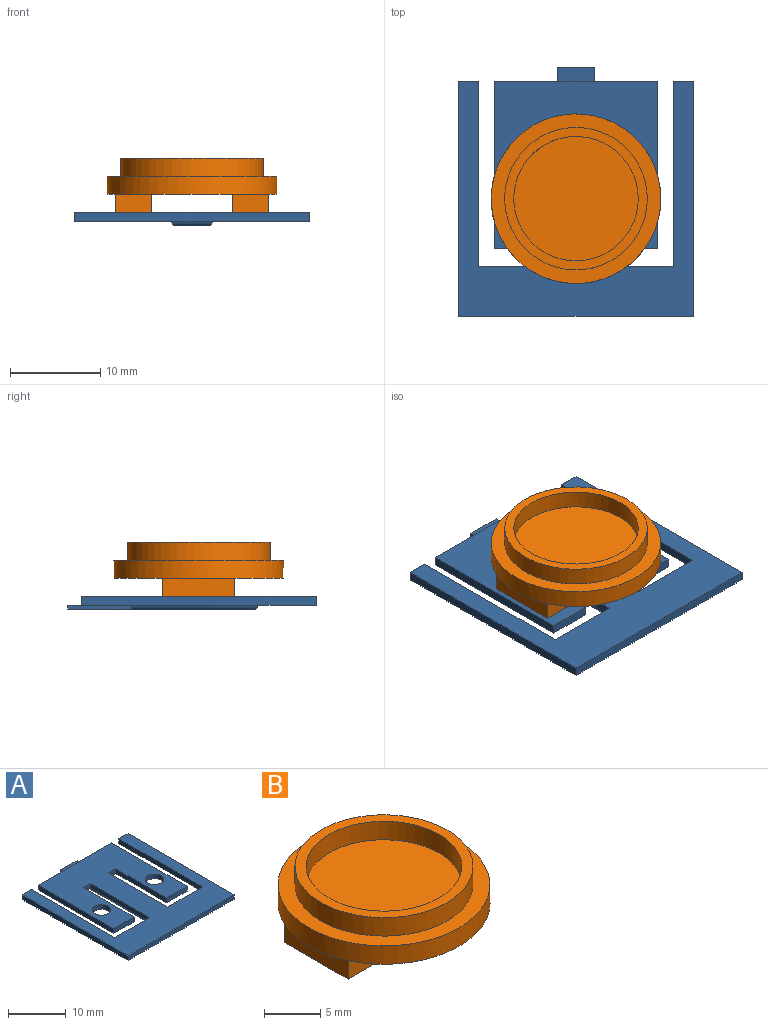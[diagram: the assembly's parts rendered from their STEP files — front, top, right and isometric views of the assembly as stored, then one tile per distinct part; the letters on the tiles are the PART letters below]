
ASSEMBLY  parts=2 mates=1
PART A: 36 faces, bbox 26x27.5x1.5 mm
  f0: plane 26x26mm, normal (0,0,-1), area 239.8mm2, adj f2,f3,f4,f5,f6,f7,f8,f18
  f1: plane 18.5x7mm, normal (0,0,-1), area 96.3mm2, adj f13,f14,f15,f16,f17,f21,f26,f27
  f2: plane 26x1mm, normal (-1,0,0), area 26mm2, adj f0,f3,f23,f24
  f3: plane 26x1mm, normal (0,-1,0), area 26mm2, adj f0,f2,f4,f24
  f4: plane 26x1mm, normal (1,0,0), area 26mm2, adj f0,f3,f5,f24
  f5: plane 2.25x1mm, normal (0,1,0), area 2.2mm2, adj f0,f4,f6,f24
  f6: plane 20.5x1mm, normal (-1,0,0), area 20.5mm2, adj f0,f5,f7,f24
  f7: plane 8.5x1mm, normal (0,1,0), area 8.5mm2, adj f0,f6,f8,f24
  f8: plane 14.5x1mm, normal (1,0,0), area 14.5mm2, adj f0,f7,f9,f24,f35
  f9: plane 1.75x1mm, normal (0,-1,0), area 1.8mm2, adj f8,f10,f24,f25
  f10: plane 12.5x1mm, normal (-1,0,0), area 12.5mm2, adj f9,f11,f24,f25
  f11: plane 5x1mm, normal (0,-1,0), area 5mm2, adj f10,f12,f24,f25
  f12: plane 18.5x1mm, normal (1,0,0), area 18.5mm2, adj f11,f13,f24,f25
  f13: plane 18x1mm, normal (0,1,0), area 18mm2, adj f1,f12,f14,f24,f25,f32
  f14: plane 18.5x1mm, normal (-1,0,0), area 18.5mm2, adj f1,f13,f15,f24
  f15: plane 5x1mm, normal (0,-1,0), area 5mm2, adj f1,f14,f16,f24
  f16: plane 12.5x1mm, normal (1,0,0), area 12.5mm2, adj f1,f15,f17,f24
  f17: plane 1.75x1mm, normal (0,-1,0), area 1.7mm2, adj f1,f16,f18,f24
  f18: plane 14.5x1mm, normal (-1,0,0), area 14.5mm2, adj f0,f17,f19,f24,f33
  f19: plane 8.5x1mm, normal (0,1,0), area 8.5mm2, adj f0,f18,f20,f24
  f20: plane 20.5x1mm, normal (1,0,0), area 20.5mm2, adj f0,f19,f23,f24
  f21: cylinder r=1.6mm len=3.2mm, axis (0,0,-1), area 10.1mm2, adj f1,f24
  f22: cylinder r=1.6mm len=3.2mm, axis (0,0,-1), area 10.1mm2, adj f24,f25
  f23: plane 2.25x1mm, normal (0,1,0), area 2.3mm2, adj f0,f2,f20,f24
  f24: plane 26x26mm, normal (0,0,1), area 517.4mm2, adj f2,f3,f4,f5,f6,f7,f8,f9
  f25: plane 18.5x7mm, normal (0,0,-1), area 96.3mm2, adj f9,f10,f11,f12,f13,f22,f29,f30
  f26: plane 0.43x0.25mm, normal (0,1,0), area 0.1mm2, adj f1,f27,f33
  f27: plane 7x0.43mm, normal (-1,0,0), area 3mm2, adj f1,f26,f28,f32,f33
  f28: plane 4x0.5mm, normal (0,1,0), area 2mm2, adj f27,f29,f31,f32,f33,f35
  f29: plane 7x0.43mm, normal (1,0,0), area 3mm2, adj f25,f28,f30,f32,f35
  f30: plane 0.43x0.25mm, normal (0,1,0), area 0.1mm2, adj f25,f29,f35
  f31: plane 20.5x3.5mm, normal (0,0,-1), area 71.8mm2, adj f28,f33,f34,f35
  f32: plane 4x1.5mm, normal (0,0,1), area 6mm2, adj f13,f27,f28,f29
  f33: cylinder r=0.5mm len=21mm, axis (0,1,0), area 12.7mm2, adj f1,f18,f26,f27,f28,f31,f34
  f34: cylinder r=0.5mm len=4.5mm, axis (1,0,0), area 3.2mm2, adj f0,f31,f33,f35
  f35: cylinder r=0.5mm len=21mm, axis (0,-1,0), area 12.7mm2, adj f8,f25,f28,f29,f30,f31,f34
PART B: 23 faces, bbox 18.8x18.8x6 mm
  f0: plane 18.79x17mm, normal (0,0,-1), area 203.6mm2, adj f2,f10,f11,f12,f17,f18,f19
  f1: plane 8x0.89mm, normal (0,0,-1), area 4.8mm2, adj f2,f9
  f2: cylinder r=9.39mm len=18.79mm, axis (0,0,-1), area 118.1mm2, adj f0,f1,f3,f4
  f3: plane 18.79x18.79mm, normal (0,0,1), area 81.5mm2, adj f2,f5
  f4: plane 8x0.89mm, normal (0,0,-1), area 4.8mm2, adj f2,f16
  f5: cylinder r=7.89mm len=15.79mm, axis (0,0,-1), area 99.2mm2, adj f3,f7
  f6: cylinder r=6.89mm len=13.79mm, axis (0,0,-1), area 86.6mm2, adj f7,f8
  f7: plane 15.79x15.79mm, normal (0,0,1), area 46.5mm2, adj f5,f6
  f8: plane 13.79x13.79mm, normal (0,0,1), area 149.3mm2, adj f6
  f9: plane 8x2mm, normal (1,0,0), area 16mm2, adj f1,f10,f12,f14
  f10: plane 4x2mm, normal (0,1,0), area 8mm2, adj f0,f9,f11,f14
  f11: plane 8x2mm, normal (-1,0,0), area 16mm2, adj f0,f10,f12,f14
  f12: plane 4x2mm, normal (0,-1,0), area 8mm2, adj f0,f9,f11,f14
  f13: cylinder r=1.6mm len=3.2mm, axis (0,0,-1), area 20.1mm2, adj f14,f15
  f14: plane 8x4mm, normal (0,0,-1), area 24mm2, adj f9,f10,f11,f12,f13
  f15: plane 3.2x3.2mm, normal (0,0,-1), area 8mm2, adj f13
  f16: plane 8x2mm, normal (-1,0,0), area 16mm2, adj f4,f17,f19,f21
  f17: plane 4x2mm, normal (0,-1,0), area 8mm2, adj f0,f16,f18,f21
  f18: plane 8x2mm, normal (1,0,0), area 16mm2, adj f0,f17,f19,f21
  f19: plane 4x2mm, normal (0,1,0), area 8mm2, adj f0,f16,f18,f21
  f20: cylinder r=1.6mm len=3.2mm, axis (0,0,-1), area 20.1mm2, adj f21,f22
  f21: plane 8x4mm, normal (0,0,-1), area 24mm2, adj f16,f17,f18,f19,f20
  f22: plane 3.2x3.2mm, normal (0,0,-1), area 8mm2, adj f20
PLACE A at identity fixed
PLACE B at identity
MATE fastened B.f20 <-> A.f21  axis (0,0,-1) through (6.5,13,1)mm
